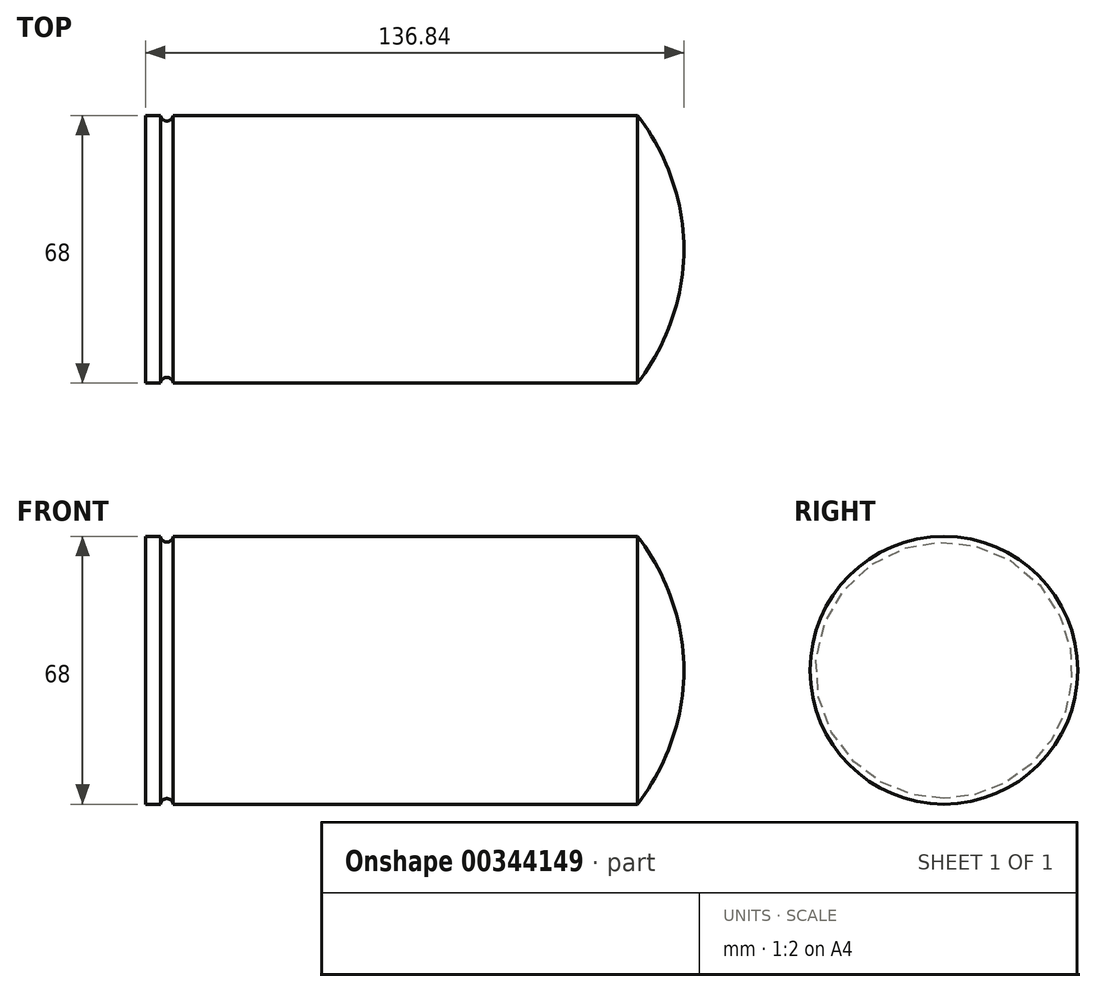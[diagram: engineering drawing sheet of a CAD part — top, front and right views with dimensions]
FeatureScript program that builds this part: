
annotation { "Feature Type Name" : "Feature", "Feature Type Description" : "" }
export const myFeature = defineFeature(function(context is Context, id is Id, definition is map)
    precondition{}
    {
        {
            var Q0;
            Q0=qCreatedBy(makeId("Front.planeOp"),FACE);
            var sketch = newSketch(context, id + "F0", { "sketchPlane" : qUnion([Q0])});
            skLineSegment(sketch, "E0.bottom", {"start": v(62.5, 17) * mm, "end": v(-62.5, 17) * mm});
            skLineSegment(sketch, "E0.top", {"start": v(62.5, -17) * mm, "end": v(-62.5, -17) * mm});
            skLineSegment(sketch, "E0.left", {"start": v(62.5, 17) * mm, "end": v(62.5, -17) * mm});
            skLineSegment(sketch, "E0.right", {"start": v(-62.5, 17) * mm, "end": v(-62.5, -17) * mm});
            skPoint(sketch, "E0.middle", {"position": v(0, 0) * mm});
            skLineSegment(sketch, "E1", {"start": v(62.5, -17) * mm, "end": v(62.5, -17) * mm});
            skLineSegment(sketch, "E2", {"start": v(62.5, -17) * mm, "end": v(74.34, -17) * mm});
            skArc(sketch, "E3", {"start": v(74.34, -17) * mm, "mid": v(71.2, 0.97) * mm, "end": v(62.5, 17) * mm});
            skArc(sketch, "E4", {"start": v(-58.67, 17) * mm, "mid": v(-57.07, 15.58) * mm, "end": v(-55.47, 17) * mm});
            skArc(sketch, "E5", {"start": v(-53.67, 15.4) * mm, "mid": v(-52.07, 13.98) * mm, "end": v(-50.47, 15.4) * mm});
            skSolve(sketch);
        }
        {
            var Q0;
            Q0=makeQuery(id+"F0.imprint","IMPRINT",FACE,{"disambiguationData":[TD([[makeQuery(id+"F0.imprint","IMPRINT",EDGE,{"derivedFrom":sQuery(id+"F0.wireOp",EDGE,"E0.left")}),1.0]])]});
            var Q1;
            Q1=makeQuery(id+"F0.imprint","IMPRINT",FACE,{"disambiguationData":[TD([[makeQuery(id+"F0.imprint","IMPRINT",EDGE,{"derivedFrom":sQuery(id+"F0.wireOp",EDGE,"E0.top")}),-1.0]])]});
            var Q2;
            Q2=sQuery(id+"F0.wireOp",EDGE,"E0.top");
            revolve(context, id + "F1", {"entities" : qUnion([Q0, Q1]), "axis" : qUnion([Q2]), "revolveType" : RevolveType.FULL});
        }
    });
